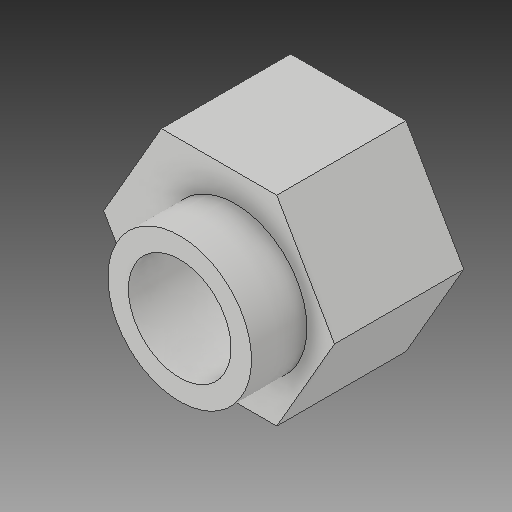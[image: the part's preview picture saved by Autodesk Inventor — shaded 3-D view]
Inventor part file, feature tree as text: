
AUTODESK INVENTOR PART (.ipt)
format: ipt  version: 2018 (Build 220112000, 112)  size: 128,000 bytes
history: native  units: mm
features: extrude x3, sketch x3, other x3, reference x1, projected_geometry x1
ambient origin geometry x8: Origin, YZ Plane, XZ Plane, XY Plane, X Axis, Y Axis, Z Axis, Center Point
bodies: Solid1 (feature_tree)
feature tree (11):
  extrude  "Extrusion1"  Depth=6.3mm TaperAngle=0.0deg
  extrude  "Extrusion2"  Depth=2.7mm TaperAngle=0.0deg
  extrude  "Extrusion3"  [1 undecoded]
  sketch  "Sketch1"  dims[d0=5.625mm d1=6.3mm d2=0.0mm]
  sketch  "Sketch2"  dims[d3=7.0mm d4=2.7mm d5=0.0mm]
  reference  "Reference2"
  sketch  "Sketch3"  dims[d6=2.7mm d7=0.0mm]
  projected_geometry  "Projected Loop1"
  other  "<userpath>\OneDrive\SL-Inventor\SL-Beast 3D Printer\DelrinY-Wheel-Bottom.iam"
  other  "DelrinY-Wheel-Bottom.iam"
  other  "Forged Socket Head Cap Screw - Metric M5x0.8 x 35:1"
note: 1 required parameter value undecoded (feature->parameter linkage not recoverable at this tier; creation-order binding heuristic only, values carry confidence <= 0.55)
